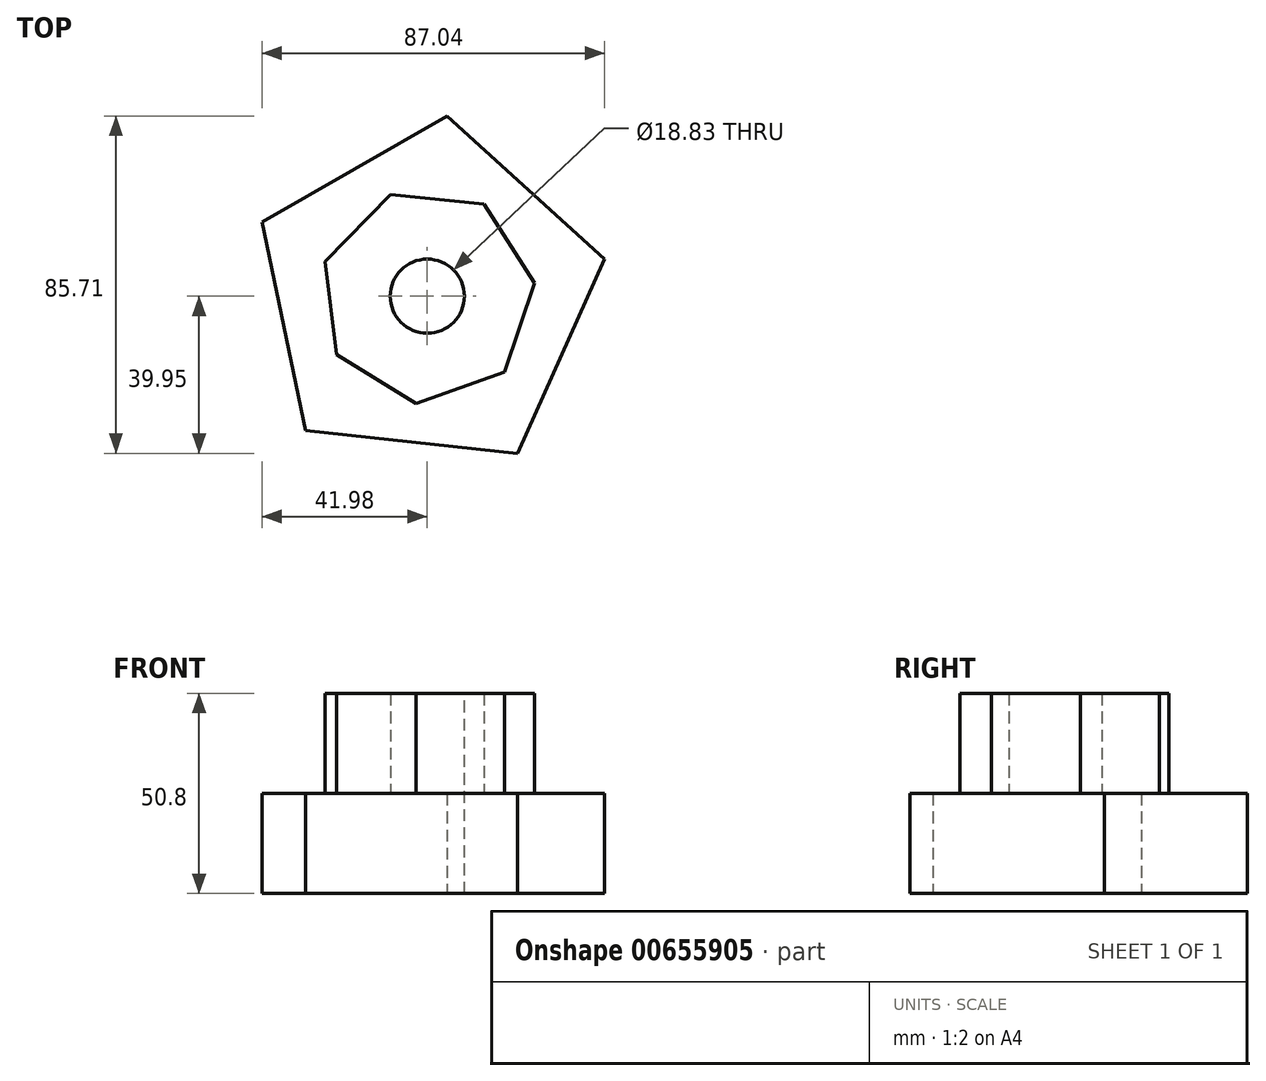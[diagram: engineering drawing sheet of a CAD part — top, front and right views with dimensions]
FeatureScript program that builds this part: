
annotation { "Feature Type Name" : "Feature", "Feature Type Description" : "" }
export const myFeature = defineFeature(function(context is Context, id is Id, definition is map)
    precondition{}
    {
        {
            var Q0;
            Q0=qCreatedBy(makeId("Top.planeOp"),FACE);
            var sketch = newSketch(context, id + "F0", { "sketchPlane" : qUnion([Q0])});
            skCircle(sketch, "E0.cCircle", {"center": v(0, 0) * mm, "radius": 37.24 * mm, "construction": true});
            skLineSegment(sketch, "E0.0", {"start": v(-41.98, 18.88) * mm, "end": v(4.98, 45.76) * mm});
            skLineSegment(sketch, "E0.1", {"start": v(4.98, 45.76) * mm, "end": v(45.06, 9.4) * mm});
            skLineSegment(sketch, "E0.2", {"start": v(45.06, 9.4) * mm, "end": v(22.87, -39.95) * mm});
            skLineSegment(sketch, "E0.3", {"start": v(22.87, -39.95) * mm, "end": v(-30.93, -34.1) * mm});
            skLineSegment(sketch, "E0.4", {"start": v(-30.93, -34.1) * mm, "end": v(-41.98, 18.88) * mm});
            skPoint(sketch, "E0.0.midPoint", {"position": v(-18.5, 32.32) * mm});
            skSolve(sketch);
        }
        {
            var Q0;
            Q0=makeQuery(id+"F0.imprint","IMPRINT",FACE,{"disambiguationData":[TD([[makeQuery(id+"F0.imprint","IMPRINT",EDGE,{"derivedFrom":sQuery(id+"F0.wireOp",EDGE,"E0.0")}),-1.0]])]});
            extrude(context, id + "F1", {"entities" : qUnion([Q0]), "depth" : 25.4 * mm, "offsetDistance" : 25.4 * mm});
        }
        {
            var Q0;
            Q0=makeQuery(id+"F1.opExtrude","CAP_FACE",FACE,{"disambiguationData":[OSD([sQuery(id+"F0.wireOp",EDGE,"E0.0"),sQuery(id+"F0.wireOp",EDGE,"E0.1"),sQuery(id+"F0.wireOp",EDGE,"E0.2"),sQuery(id+"F0.wireOp",EDGE,"E0.3"),sQuery(id+"F0.wireOp",EDGE,"E0.4")])],"isStart":false});
            var sketch = newSketch(context, id + "F2", { "sketchPlane" : qUnion([Q0])});
            skCircle(sketch, "E1.cCircle", {"center": v(0, 0) * mm, "radius": 24.73 * mm, "construction": true});
            skLineSegment(sketch, "E1.0", {"start": v(-25.99, 8.82) * mm, "end": v(-9.3, 25.82) * mm});
            skLineSegment(sketch, "E1.1", {"start": v(-9.3, 25.82) * mm, "end": v(14.38, 23.37) * mm});
            skLineSegment(sketch, "E1.2", {"start": v(14.38, 23.37) * mm, "end": v(27.24, 3.33) * mm});
            skLineSegment(sketch, "E1.3", {"start": v(27.24, 3.33) * mm, "end": v(19.59, -19.22) * mm});
            skLineSegment(sketch, "E1.4", {"start": v(19.59, -19.22) * mm, "end": v(-2.81, -27.3) * mm});
            skLineSegment(sketch, "E1.5", {"start": v(-2.81, -27.3) * mm, "end": v(-23.1, -14.82) * mm});
            skLineSegment(sketch, "E1.6", {"start": v(-23.1, -14.82) * mm, "end": v(-25.99, 8.82) * mm});
            skPoint(sketch, "E1.0.midPoint", {"position": v(-17.65, 17.32) * mm});
            skSolve(sketch);
        }
        {
            var Q0;
            Q0=makeQuery(id+"F2.imprint","IMPRINT",FACE,{"disambiguationData":[TD([[makeQuery(id+"F2.imprint","IMPRINT",EDGE,{"derivedFrom":sQuery(id+"F2.wireOp",EDGE,"E1.0")}),-1.0]])]});
            extrude(context, id + "F3", {"entities" : qUnion([Q0]), "operationType" : NewBodyOperationType.ADD, "depth" : 25.4 * mm, "offsetDistance" : 25.4 * mm});
        }
        {
            var Q0;
            Q0=makeQuery(id+"F3.opExtrude","CAP_FACE",FACE,{"disambiguationData":[OSD([sQuery(id+"F2.wireOp",EDGE,"E1.0"),sQuery(id+"F2.wireOp",EDGE,"E1.1"),sQuery(id+"F2.wireOp",EDGE,"E1.2"),sQuery(id+"F2.wireOp",EDGE,"E1.3"),sQuery(id+"F2.wireOp",EDGE,"E1.4"),sQuery(id+"F2.wireOp",EDGE,"E1.5"),sQuery(id+"F2.wireOp",EDGE,"E1.6")])],"isStart":false});
            var sketch = newSketch(context, id + "F4", { "sketchPlane" : qUnion([Q0])});
            skCircle(sketch, "E2", {"center": v(0, 0) * mm, "radius": 9.42 * mm});
            skSolve(sketch);
        }
        {
            var Q0;
            Q0=makeQuery(id+"F4.imprint","IMPRINT",FACE,{"disambiguationData":[TD([[makeQuery(id+"F4.imprint","IMPRINT",EDGE,{"derivedFrom":sQuery(id+"F4.wireOp",EDGE,"E2")}),1.0]])]});
            extrude(context, id + "F5", {"entities" : qUnion([Q0]), "operationType" : NewBodyOperationType.REMOVE, "oppositeDirection" : true, "depth" : 94.74 * mm, "offsetDistance" : 25.4 * mm});
        }
    });
